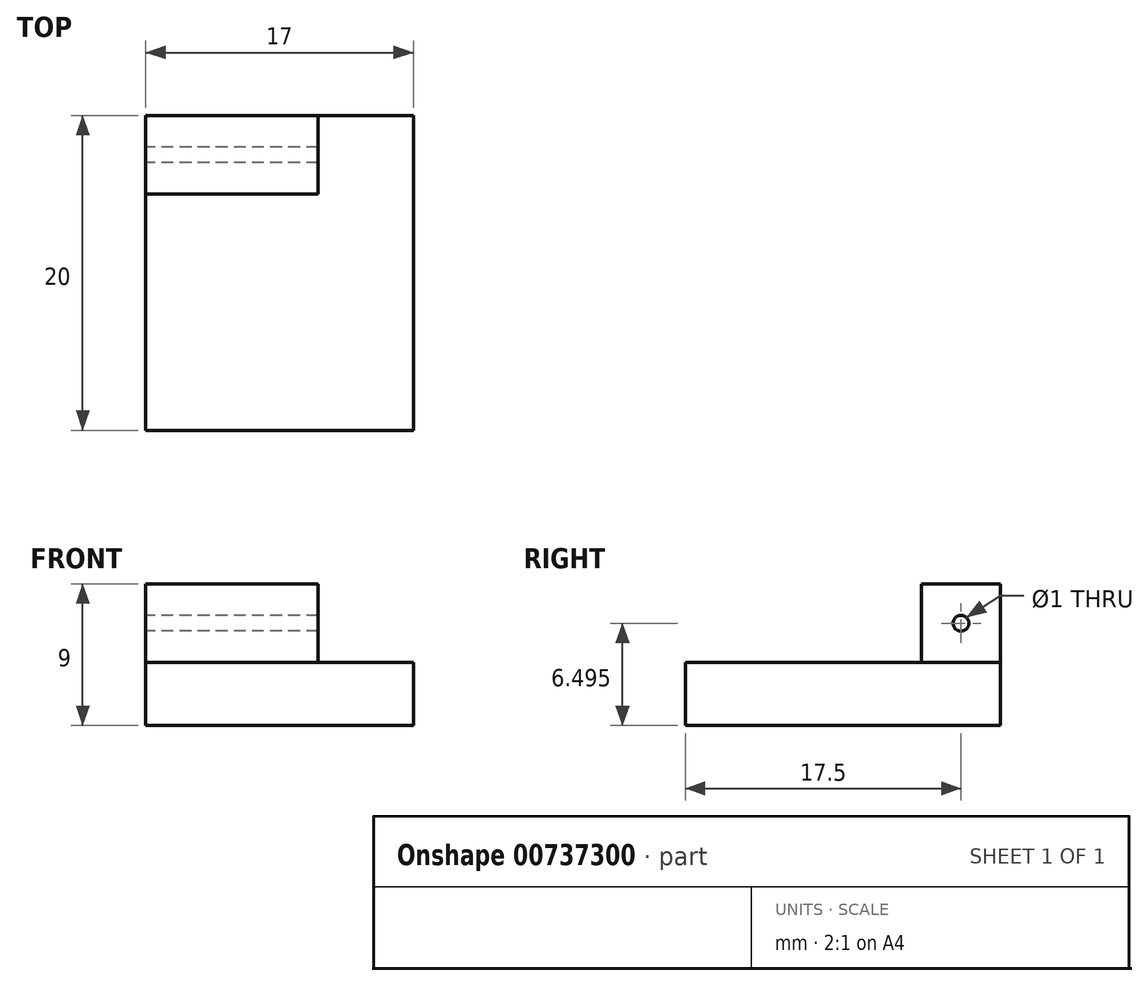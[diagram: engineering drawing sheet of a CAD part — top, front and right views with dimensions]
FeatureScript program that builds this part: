
annotation { "Feature Type Name" : "Feature", "Feature Type Description" : "" }
export const myFeature = defineFeature(function(context is Context, id is Id, definition is map)
    precondition{}
    {
        {
            var Q0;
            Q0=qCreatedBy(makeId("Front.planeOp"),FACE);
            var sketch = newSketch(context, id + "F0", { "sketchPlane" : qUnion([Q0])});
            skLineSegment(sketch, "E0.bottom", {"start": v(-9.77, 2.77) * mm, "end": v(7.23, 2.77) * mm});
            skLineSegment(sketch, "E0.top", {"start": v(-9.77, -1.23) * mm, "end": v(7.23, -1.23) * mm});
            skLineSegment(sketch, "E0.left", {"start": v(-9.77, 2.77) * mm, "end": v(-9.77, -1.23) * mm});
            skLineSegment(sketch, "E0.right", {"start": v(7.23, 2.77) * mm, "end": v(7.23, -1.23) * mm});
            skSolve(sketch);
        }
        {
            var Q0;
            Q0 = qSketchRegion(id + "F0", true);
            extrude(context, id + "F1", {"entities" : qUnion([Q0]), "depth" : 20 * mm, "offsetDistance" : 25 * mm});
        }
        {
            var Q0;
            Q0=makeQuery(id+"F1.opExtrude","SWEPT_FACE",FACE,{"disambiguationData":[OSD([sQuery(id+"F0.wireOp",EDGE,"E0.left")])]});
            var sketch = newSketch(context, id + "F2", { "sketchPlane" : qUnion([Q0])});
            skLineSegment(sketch, "E1.bottom", {"start": v(0, 2.77) * mm, "end": v(5, 2.77) * mm});
            skLineSegment(sketch, "E1.top", {"start": v(0, 7.77) * mm, "end": v(5, 7.77) * mm});
            skLineSegment(sketch, "E1.left", {"start": v(0, 2.77) * mm, "end": v(0, 7.77) * mm});
            skLineSegment(sketch, "E1.right", {"start": v(5, 2.77) * mm, "end": v(5, 7.77) * mm});
            skCircle(sketch, "E2", {"center": v(2.5, 5.27) * mm, "radius": 0.5 * mm});
            skSolve(sketch);
        }
        {
            var Q0;
            Q0 = qSketchRegion(id + "F2", true);
            extrude(context, id + "F3", {"entities" : qUnion([Q0]), "operationType" : NewBodyOperationType.ADD, "oppositeDirection" : true, "depth" : 10.95 * mm, "offsetDistance" : 25 * mm});
        }
    });
